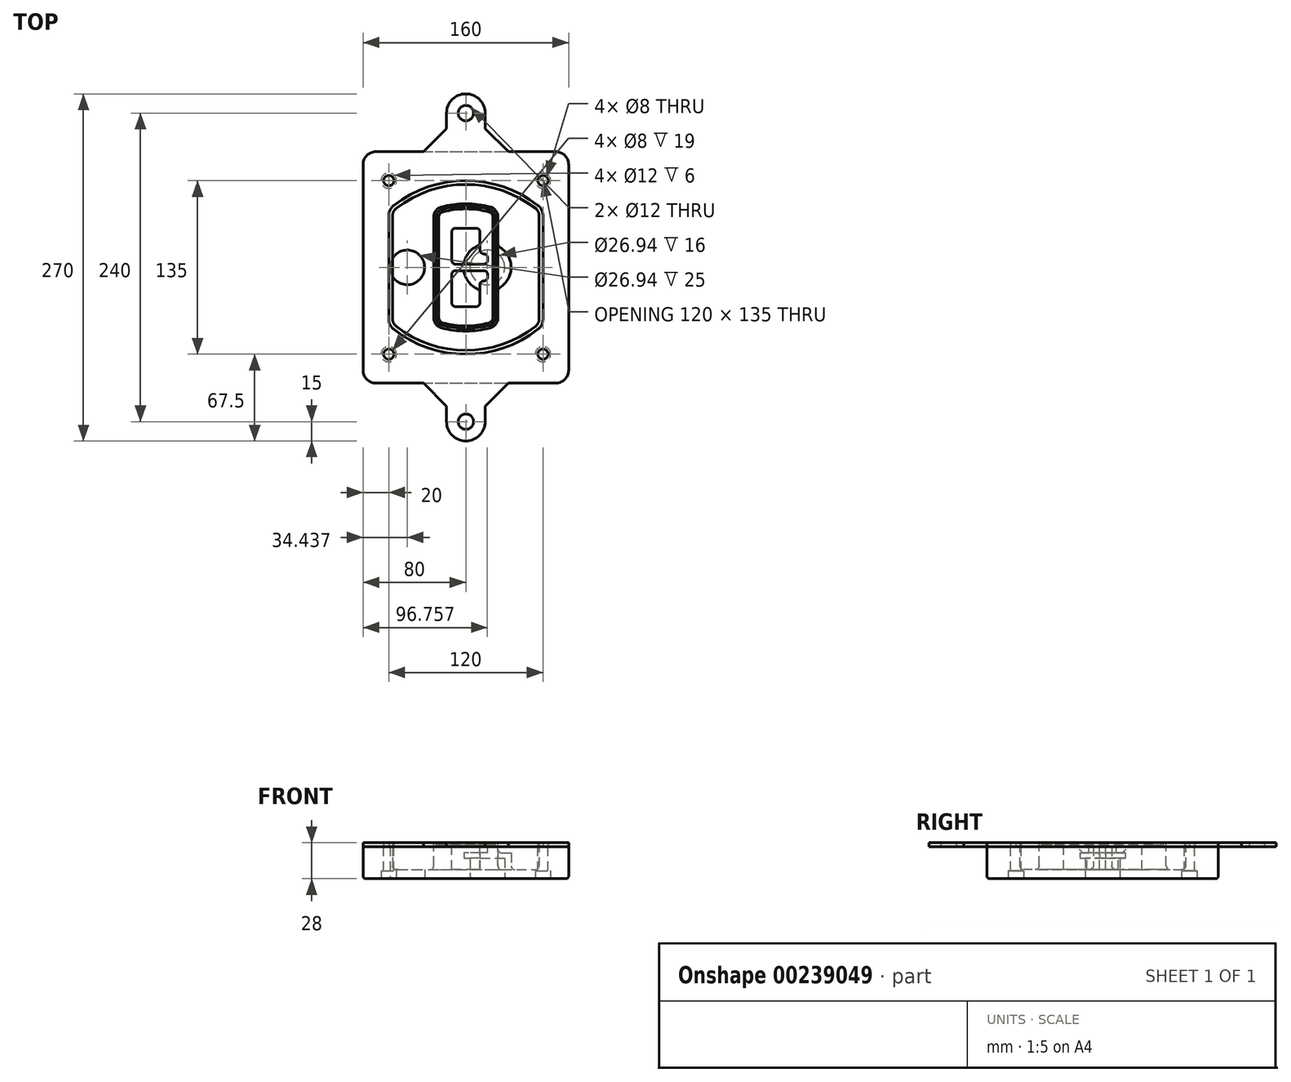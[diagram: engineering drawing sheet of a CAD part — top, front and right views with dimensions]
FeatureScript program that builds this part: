
annotation { "Feature Type Name" : "Feature", "Feature Type Description" : "" }
export const myFeature = defineFeature(function(context is Context, id is Id, definition is map)
    precondition{}
    {
        {
            var Q0;
            Q0=qCreatedBy(makeId("Top.planeOp"),FACE);
            var sketch = newSketch(context, id + "F0", { "sketchPlane" : qUnion([Q0])});
            skPoint(sketch, "E0.rect.middle", {"position": v(0, 0) * mm});
            skLineSegment(sketch, "E1.bottom", {"start": v(-70, -90) * mm, "end": v(70, -90) * mm});
            skLineSegment(sketch, "E1.top", {"start": v(-70, 90) * mm, "end": v(70, 90) * mm});
            skLineSegment(sketch, "E1.left", {"start": v(-80, -80) * mm, "end": v(-80, 80) * mm});
            skLineSegment(sketch, "E1.right", {"start": v(80, -80) * mm, "end": v(80, 80) * mm});
            skLineSegment(sketch, "E2", {"start": v(-80, 90) * mm, "end": v(80, -90) * mm, "construction": true});
            skLineSegment(sketch, "E3", {"start": v(80, 90) * mm, "end": v(-80, -90) * mm, "construction": true});
            skCircle(sketch, "E4", {"center": v(-60, 67.5) * mm, "radius": 4 * mm});
            skCircle(sketch, "E5", {"center": v(60, 67.5) * mm, "radius": 4 * mm});
            skCircle(sketch, "E6", {"center": v(60, -67.5) * mm, "radius": 4 * mm});
            skCircle(sketch, "E7", {"center": v(-60, -67.5) * mm, "radius": 4 * mm});
            skLineSegment(sketch, "E8", {"start": v(-60, 67.5) * mm, "end": v(60, 67.5) * mm, "construction": true});
            skLineSegment(sketch, "E9", {"start": v(60, 67.5) * mm, "end": v(60, -67.5) * mm, "construction": true});
            skLineSegment(sketch, "E10", {"start": v(60, -67.5) * mm, "end": v(-60, -67.5) * mm, "construction": true});
            skLineSegment(sketch, "E11", {"start": v(-60, -67.5) * mm, "end": v(-60, 67.5) * mm, "construction": true});
            skLineSegment(sketch, "E12", {"start": v(-60, 40.3) * mm, "end": v(-60, -40.3) * mm});
            skLineSegment(sketch, "E13", {"start": v(60, 40.3) * mm, "end": v(60, -40.3) * mm});
            skArc(sketch, "E14", {"start": v(56.15, 48.18) * mm, "mid": v(0, 67.5) * mm, "end": v(-56.15, 48.18) * mm});
            skArc(sketch, "E15", {"start": v(-56.15, -48.18) * mm, "mid": v(0, -67.5) * mm, "end": v(56.15, -48.18) * mm});
            skLineSegment(sketch, "E16", {"start": v(-60, 0) * mm, "end": v(60, 0) * mm, "construction": true});
            skPoint(sketch, "E17.visualSharp", {"position": v(-60, -45) * mm});
            skArc(sketch, "E17.filletArc", {"start": v(-60, -40.3) * mm, "mid": v(-58.99, -44.68) * mm, "end": v(-56.15, -48.18) * mm});
            skPoint(sketch, "E18.visualSharp", {"position": v(-60, 45) * mm});
            skArc(sketch, "E18.filletArc", {"start": v(-56.15, 48.18) * mm, "mid": v(-58.99, 44.68) * mm, "end": v(-60, 40.3) * mm});
            skPoint(sketch, "E19.visualSharp", {"position": v(60, 45) * mm});
            skArc(sketch, "E19.filletArc", {"start": v(60, 40.3) * mm, "mid": v(58.99, 44.68) * mm, "end": v(56.15, 48.18) * mm});
            skPoint(sketch, "E20.visualSharp", {"position": v(60, -45) * mm});
            skArc(sketch, "E20.filletArc", {"start": v(56.15, -48.18) * mm, "mid": v(58.99, -44.68) * mm, "end": v(60, -40.3) * mm});
            skPoint(sketch, "E21.visualSharp", {"position": v(-80, 90) * mm});
            skArc(sketch, "E21.filletArc", {"start": v(-70, 90) * mm, "mid": v(-77.07, 87.07) * mm, "end": v(-80, 80) * mm});
            skPoint(sketch, "E22.visualSharp", {"position": v(80, 90) * mm});
            skArc(sketch, "E22.filletArc", {"start": v(80, 80) * mm, "mid": v(77.07, 87.07) * mm, "end": v(70, 90) * mm});
            skPoint(sketch, "E23.visualSharp", {"position": v(80, -90) * mm});
            skArc(sketch, "E23.filletArc", {"start": v(70, -90) * mm, "mid": v(77.07, -87.07) * mm, "end": v(80, -80) * mm});
            skPoint(sketch, "E24.visualSharp", {"position": v(-80, -90) * mm});
            skArc(sketch, "E24.filletArc", {"start": v(-80, -80) * mm, "mid": v(-77.07, -87.07) * mm, "end": v(-70, -90) * mm});
            skArc(sketch, "E25.0", {"start": v(57, 40.3) * mm, "mid": v(56.3, 43.36) * mm, "end": v(54.3, 45.81) * mm});
            skLineSegment(sketch, "E25.1", {"start": v(57, 40.3) * mm, "end": v(57, -40.3) * mm});
            skArc(sketch, "E25.2", {"start": v(54.3, -45.81) * mm, "mid": v(56.3, -43.36) * mm, "end": v(57, -40.3) * mm});
            skArc(sketch, "E25.3", {"start": v(-54.3, -45.81) * mm, "mid": v(0, -64.5) * mm, "end": v(54.3, -45.81) * mm});
            skArc(sketch, "E25.4", {"start": v(-57, -40.3) * mm, "mid": v(-56.3, -43.36) * mm, "end": v(-54.3, -45.81) * mm});
            skArc(sketch, "E25.5", {"start": v(54.3, 45.81) * mm, "mid": v(0, 64.5) * mm, "end": v(-54.3, 45.81) * mm});
            skLineSegment(sketch, "E25.6", {"start": v(-57, 40.3) * mm, "end": v(-57, -40.3) * mm});
            skArc(sketch, "E25.7", {"start": v(-54.3, 45.81) * mm, "mid": v(-56.3, 43.36) * mm, "end": v(-57, 40.3) * mm});
            skArc(sketch, "E26.0", {"start": v(-58.62, 51.33) * mm, "mid": v(-62.58, 46.43) * mm, "end": v(-64, 40.3) * mm});
            skArc(sketch, "E26.1", {"start": v(58.62, 51.33) * mm, "mid": v(0, 71.5) * mm, "end": v(-58.62, 51.33) * mm});
            skArc(sketch, "E26.2", {"start": v(64, 40.3) * mm, "mid": v(62.58, 46.43) * mm, "end": v(58.62, 51.33) * mm});
            skLineSegment(sketch, "E26.3", {"start": v(64, 40.3) * mm, "end": v(64, -40.3) * mm});
            skArc(sketch, "E26.4", {"start": v(58.62, -51.33) * mm, "mid": v(62.58, -46.43) * mm, "end": v(64, -40.3) * mm});
            skLineSegment(sketch, "E26.5", {"start": v(-64, 40.3) * mm, "end": v(-64, -40.3) * mm});
            skArc(sketch, "E26.6", {"start": v(-58.62, -51.33) * mm, "mid": v(0, -71.5) * mm, "end": v(58.62, -51.33) * mm});
            skArc(sketch, "E26.7", {"start": v(-64, -40.3) * mm, "mid": v(-62.58, -46.43) * mm, "end": v(-58.62, -51.33) * mm});
            skSolve(sketch);
        }
        {
            var Q0;
            Q0=makeQuery(id+"F0.imprint","IMPRINT",FACE,{"disambiguationData":[TD([[makeQuery(id+"F0.imprint","IMPRINT",EDGE,{"derivedFrom":sQuery(id+"F0.wireOp",EDGE,"E1.bottom")}),1.0]])]});
            var Q1;
            Q1=makeQuery(id+"F0.imprint","IMPRINT",FACE,{"disambiguationData":[TD([[makeQuery(id+"F0.imprint","IMPRINT",EDGE,{"derivedFrom":sQuery(id+"F0.wireOp",EDGE,"E12")}),1.0]])]});
            var Q2;
            Q2=makeQuery(id+"F0.imprint","IMPRINT",FACE,{"disambiguationData":[TD([[makeQuery(id+"F0.imprint","IMPRINT",EDGE,{"derivedFrom":sQuery(id+"F0.wireOp",EDGE,"E25.0")}),1.0]])]});
            var Q3;
            Q3=makeQuery(id+"F0.imprint","IMPRINT",FACE,{"disambiguationData":[TD([[makeQuery(id+"F0.imprint","IMPRINT",EDGE,{"derivedFrom":sQuery(id+"F0.wireOp",EDGE,"E12")}),-1.0]])]});
            extrude(context, id + "F1", {"entities" : qUnion([Q0, Q1, Q2, Q3]), "oppositeDirection" : true, "depth" : 25 * mm});
        }
        {
            var Q0;
            Q0=makeQuery(id+"F0.imprint","IMPRINT",FACE,{"disambiguationData":[TD([[makeQuery(id+"F0.imprint","IMPRINT",EDGE,{"derivedFrom":sQuery(id+"F0.wireOp",EDGE,"E12")}),1.0]])]});
            extrude(context, id + "F2", {"entities" : qUnion([Q0]), "operationType" : NewBodyOperationType.ADD, "depth" : 3 * mm});
        }
        {
            var Q0;
            Q0=makeQuery(id+"F0.imprint","IMPRINT",FACE,{"disambiguationData":[TD([[makeQuery(id+"F0.imprint","IMPRINT",EDGE,{"derivedFrom":sQuery(id+"F0.wireOp",EDGE,"E25.0")}),1.0]])]});
            extrude(context, id + "F3", {"entities" : qUnion([Q0]), "operationType" : NewBodyOperationType.REMOVE, "oppositeDirection" : true, "depth" : 18 * mm});
        }
        {
            var Q0;
            Q0=makeQuery(id+"F2.opExtrude","CAP_FACE",FACE,{"disambiguationData":[OSD([sQuery(id+"F0.wireOp",EDGE,"E12"),sQuery(id+"F0.wireOp",EDGE,"E13"),sQuery(id+"F0.wireOp",EDGE,"E14"),sQuery(id+"F0.wireOp",EDGE,"E15"),sQuery(id+"F0.wireOp",EDGE,"E17.filletArc"),sQuery(id+"F0.wireOp",EDGE,"E18.filletArc"),sQuery(id+"F0.wireOp",EDGE,"E19.filletArc"),sQuery(id+"F0.wireOp",EDGE,"E20.filletArc"),sQuery(id+"F0.wireOp",EDGE,"E25.0"),sQuery(id+"F0.wireOp",EDGE,"E25.1"),sQuery(id+"F0.wireOp",EDGE,"E25.2"),sQuery(id+"F0.wireOp",EDGE,"E25.3"),sQuery(id+"F0.wireOp",EDGE,"E25.4"),sQuery(id+"F0.wireOp",EDGE,"E25.5"),sQuery(id+"F0.wireOp",EDGE,"E25.6"),sQuery(id+"F0.wireOp",EDGE,"E25.7")])],"isStart":false});
            var sketch = newSketch(context, id + "F4", { "sketchPlane" : qUnion([Q0])});
            skArc(sketch, "E27.0", {"start": v(-19.08, -46.97) * mm, "mid": v(0, -49.5) * mm, "end": v(19.08, -46.97) * mm});
            skArc(sketch, "E28.0", {"start": v(19.08, 46.97) * mm, "mid": v(0, 49.5) * mm, "end": v(-19.08, 46.97) * mm});
            skLineSegment(sketch, "E29", {"start": v(-25, 39.25) * mm, "end": v(-25, -39.25) * mm});
            skLineSegment(sketch, "E30", {"start": v(25, 39.25) * mm, "end": v(25, -39.25) * mm});
            skLineSegment(sketch, "E31", {"start": v(-25, 45.1) * mm, "end": v(25, 45.1) * mm, "construction": true});
            skLineSegment(sketch, "E32", {"start": v(-25, -45.1) * mm, "end": v(25, -45.1) * mm, "construction": true});
            skPoint(sketch, "E33.visualSharp", {"position": v(-25, 45.1) * mm});
            skArc(sketch, "E33.filletArc", {"start": v(-19.08, 46.97) * mm, "mid": v(-23.35, 44.11) * mm, "end": v(-25, 39.25) * mm});
            skPoint(sketch, "E34.visualSharp", {"position": v(25, 45.1) * mm});
            skArc(sketch, "E34.filletArc", {"start": v(25, 39.25) * mm, "mid": v(23.35, 44.11) * mm, "end": v(19.08, 46.97) * mm});
            skPoint(sketch, "E35.visualSharp", {"position": v(25, -45.1) * mm});
            skArc(sketch, "E35.filletArc", {"start": v(19.08, -46.97) * mm, "mid": v(23.35, -44.11) * mm, "end": v(25, -39.25) * mm});
            skPoint(sketch, "E36.visualSharp", {"position": v(-25, -45.1) * mm});
            skArc(sketch, "E36.filletArc", {"start": v(-25, -39.25) * mm, "mid": v(-23.35, -44.11) * mm, "end": v(-19.08, -46.97) * mm});
            skArc(sketch, "E37.0", {"start": v(54.3, 45.81) * mm, "mid": v(0, 64.5) * mm, "end": v(-54.3, 45.81) * mm});
            skArc(sketch, "E37.1", {"start": v(-54.3, 45.81) * mm, "mid": v(-56.3, 43.36) * mm, "end": v(-57, 40.3) * mm});
            skLineSegment(sketch, "E37.2", {"start": v(-57, 40.3) * mm, "end": v(-57, -40.3) * mm});
            skArc(sketch, "E37.3", {"start": v(-57, -40.3) * mm, "mid": v(-56.3, -43.36) * mm, "end": v(-54.3, -45.81) * mm});
            skArc(sketch, "E37.4", {"start": v(-54.3, -45.81) * mm, "mid": v(0, -64.5) * mm, "end": v(54.3, -45.81) * mm});
            skArc(sketch, "E37.5", {"start": v(54.3, -45.81) * mm, "mid": v(56.3, -43.36) * mm, "end": v(57, -40.3) * mm});
            skLineSegment(sketch, "E37.6", {"start": v(57, 40.3) * mm, "end": v(57, -40.3) * mm});
            skArc(sketch, "E37.7", {"start": v(57, 40.3) * mm, "mid": v(56.3, 43.36) * mm, "end": v(54.3, 45.81) * mm});
            skLineSegment(sketch, "E38.0", {"start": v(23, 39.25) * mm, "end": v(23, -39.25) * mm});
            skArc(sketch, "E38.1", {"start": v(18.56, -45.04) * mm, "mid": v(21.76, -42.9) * mm, "end": v(23, -39.25) * mm});
            skArc(sketch, "E38.2", {"start": v(-18.56, -45.04) * mm, "mid": v(0, -47.5) * mm, "end": v(18.56, -45.04) * mm});
            skArc(sketch, "E38.3", {"start": v(-23, -39.25) * mm, "mid": v(-21.76, -42.9) * mm, "end": v(-18.56, -45.04) * mm});
            skLineSegment(sketch, "E38.4", {"start": v(-23, 39.25) * mm, "end": v(-23, -39.25) * mm});
            skArc(sketch, "E38.5", {"start": v(23, 39.25) * mm, "mid": v(21.76, 42.9) * mm, "end": v(18.56, 45.04) * mm});
            skArc(sketch, "E38.6", {"start": v(-18.56, 45.04) * mm, "mid": v(-21.76, 42.9) * mm, "end": v(-23, 39.25) * mm});
            skArc(sketch, "E38.7", {"start": v(18.56, 45.04) * mm, "mid": v(0, 47.5) * mm, "end": v(-18.56, 45.04) * mm});
            skArc(sketch, "E39.0", {"start": v(21, 39.25) * mm, "mid": v(20.18, 41.68) * mm, "end": v(18.04, 43.1) * mm});
            skLineSegment(sketch, "E39.1", {"start": v(21, 39.25) * mm, "end": v(21, -39.25) * mm});
            skArc(sketch, "E39.2", {"start": v(18.04, -43.1) * mm, "mid": v(20.18, -41.68) * mm, "end": v(21, -39.25) * mm});
            skArc(sketch, "E39.3", {"start": v(-18.04, -43.1) * mm, "mid": v(0, -45.5) * mm, "end": v(18.04, -43.1) * mm});
            skArc(sketch, "E39.4", {"start": v(-21, -39.25) * mm, "mid": v(-20.18, -41.68) * mm, "end": v(-18.04, -43.1) * mm});
            skArc(sketch, "E39.5", {"start": v(18.04, 43.1) * mm, "mid": v(0, 45.5) * mm, "end": v(-18.04, 43.1) * mm});
            skLineSegment(sketch, "E39.6", {"start": v(-21, 39.25) * mm, "end": v(-21, -39.25) * mm});
            skArc(sketch, "E39.7", {"start": v(-18.04, 43.1) * mm, "mid": v(-20.18, 41.68) * mm, "end": v(-21, 39.25) * mm});
            skLineSegment(sketch, "E40", {"start": v(-25, 0) * mm, "end": v(25, 0) * mm, "construction": true});
            skLineSegment(sketch, "E41", {"start": v(-11, 5.5) * mm, "end": v(-11, 27.5) * mm});
            skLineSegment(sketch, "E42", {"start": v(-8, 30.5) * mm, "end": v(8, 30.5) * mm});
            skLineSegment(sketch, "E43", {"start": v(11, 27.5) * mm, "end": v(11, 13.5) * mm});
            skLineSegment(sketch, "E44", {"start": v(14, 10.5) * mm, "end": v(14, 10.5) * mm});
            skLineSegment(sketch, "E45", {"start": v(17, 7.5) * mm, "end": v(17, 5.5) * mm});
            skLineSegment(sketch, "E46", {"start": v(14, 2.5) * mm, "end": v(-8, 2.5) * mm});
            skPoint(sketch, "E47.visualSharp", {"position": v(-11, 30.5) * mm});
            skArc(sketch, "E47.filletArc", {"start": v(-8, 30.5) * mm, "mid": v(-10.12, 29.62) * mm, "end": v(-11, 27.5) * mm});
            skPoint(sketch, "E48.visualSharp", {"position": v(11, 30.5) * mm});
            skArc(sketch, "E48.filletArc", {"start": v(11, 27.5) * mm, "mid": v(10.12, 29.62) * mm, "end": v(8, 30.5) * mm});
            skPoint(sketch, "E49.visualSharp", {"position": v(11, 10.5) * mm});
            skArc(sketch, "E49.filletArc", {"start": v(11, 13.5) * mm, "mid": v(11.88, 11.38) * mm, "end": v(14, 10.5) * mm});
            skPoint(sketch, "E50.visualSharp", {"position": v(17, 10.5) * mm});
            skArc(sketch, "E50.filletArc", {"start": v(17, 7.5) * mm, "mid": v(16.12, 9.62) * mm, "end": v(14, 10.5) * mm});
            skPoint(sketch, "E51.visualSharp", {"position": v(17, 2.5) * mm});
            skArc(sketch, "E51.filletArc", {"start": v(14, 2.5) * mm, "mid": v(16.12, 3.38) * mm, "end": v(17, 5.5) * mm});
            skPoint(sketch, "E52.visualSharp", {"position": v(-11, 2.5) * mm});
            skArc(sketch, "E52.filletArc", {"start": v(-11, 5.5) * mm, "mid": v(-10.12, 3.38) * mm, "end": v(-8, 2.5) * mm});
            skLineSegment(sketch, "E53.0.MirrorCS", {"start": v(14, -2.5) * mm, "end": v(-8, -2.5) * mm});
            skArc(sketch, "E54.0.MirrorCS", {"start": v(-11, -5.5) * mm, "mid": v(-10.12, -3.38) * mm, "end": v(-8, -2.5) * mm});
            skLineSegment(sketch, "E55.0.MirrorCS", {"start": v(-11, -5.5) * mm, "end": v(-11, -27.5) * mm});
            skArc(sketch, "E56.0.MirrorCS", {"start": v(-8, -30.5) * mm, "mid": v(-10.12, -29.62) * mm, "end": v(-11, -27.5) * mm});
            skLineSegment(sketch, "E57.0.MirrorCS", {"start": v(-8, -30.5) * mm, "end": v(8, -30.5) * mm});
            skArc(sketch, "E58.0.MirrorCS", {"start": v(11, -27.5) * mm, "mid": v(10.12, -29.62) * mm, "end": v(8, -30.5) * mm});
            skLineSegment(sketch, "E59.0.MirrorCS", {"start": v(11, -27.5) * mm, "end": v(11, -13.5) * mm});
            skArc(sketch, "E60.0.MirrorCS", {"start": v(11, -13.5) * mm, "mid": v(11.88, -11.38) * mm, "end": v(14, -10.5) * mm});
            skArc(sketch, "E61.0.MirrorCS", {"start": v(17, -7.5) * mm, "mid": v(16.12, -9.62) * mm, "end": v(14, -10.5) * mm});
            skLineSegment(sketch, "E62.0.MirrorCS", {"start": v(17, -7.5) * mm, "end": v(17, -5.5) * mm});
            skArc(sketch, "E63.0.MirrorCS", {"start": v(14, -2.5) * mm, "mid": v(16.12, -3.38) * mm, "end": v(17, -5.5) * mm});
            skSolve(sketch);
        }
        {
            var Q0;
            Q0=makeQuery(id+"F4.imprint","IMPRINT",FACE,{"disambiguationData":[TD([[makeQuery(id+"F4.imprint","IMPRINT",EDGE,{"derivedFrom":sQuery(id+"F4.wireOp",EDGE,"E27.0")}),1.0]])]});
            var Q1;
            Q1=makeQuery(id+"F4.imprint","IMPRINT",FACE,{"disambiguationData":[TD([[makeQuery(id+"F4.imprint","IMPRINT",EDGE,{"derivedFrom":sQuery(id+"F4.wireOp",EDGE,"E38.0")}),-1.0]])]});
            var Q2;
            Q2=makeQuery(id+"F4.imprint","IMPRINT",FACE,{"disambiguationData":[TD([[makeQuery(id+"F4.imprint","IMPRINT",EDGE,{"derivedFrom":sQuery(id+"F4.wireOp",EDGE,"E39.0")}),1.0]])]});
            extrude(context, id + "F5", {"entities" : qUnion([Q0, Q1, Q2]), "operationType" : NewBodyOperationType.ADD, "endBound" : BoundingType.UP_TO_NEXT, "oppositeDirection" : true, "depth" : 25 * mm});
        }
        {
            var Q0;
            Q0=makeQuery(id+"F4.imprint","IMPRINT",FACE,{"disambiguationData":[TD([[makeQuery(id+"F4.imprint","IMPRINT",EDGE,{"derivedFrom":sQuery(id+"F4.wireOp",EDGE,"E38.0")}),-1.0]])]});
            extrude(context, id + "F6", {"entities" : qUnion([Q0]), "operationType" : NewBodyOperationType.REMOVE, "oppositeDirection" : true, "depth" : 2 * mm});
        }
        {
            var Q0;
            Q0=makeQuery(id+"F1.opExtrude","CAP_FACE",FACE,{"disambiguationData":[OSD([sQuery(id+"F0.wireOp",EDGE,"E1.bottom"),sQuery(id+"F0.wireOp",EDGE,"E1.top"),sQuery(id+"F0.wireOp",EDGE,"E1.left"),sQuery(id+"F0.wireOp",EDGE,"E1.right"),sQuery(id+"F0.wireOp",EDGE,"E4"),sQuery(id+"F0.wireOp",EDGE,"E5"),sQuery(id+"F0.wireOp",EDGE,"E6"),sQuery(id+"F0.wireOp",EDGE,"E7"),sQuery(id+"F0.wireOp",EDGE,"E21.filletArc"),sQuery(id+"F0.wireOp",EDGE,"E22.filletArc"),sQuery(id+"F0.wireOp",EDGE,"E23.filletArc"),sQuery(id+"F0.wireOp",EDGE,"E24.filletArc")])],"isStart":false});
            var sketch = newSketch(context, id + "F7", { "sketchPlane" : qUnion([Q0])});
            skCircle(sketch, "E64", {"center": v(16.76, 0) * mm, "radius": 13.47 * mm});
            skCircle(sketch, "E65", {"center": v(-45.56, 0) * mm, "radius": 13.47 * mm});
            skLineSegment(sketch, "E66", {"start": v(80, 0) * mm, "end": v(-80, 0) * mm});
            skCircle(sketch, "E67", {"center": v(16.76, 0) * mm, "radius": 18.47 * mm});
            skCircle(sketch, "E68", {"center": v(60, -67.5) * mm, "radius": 6 * mm});
            skCircle(sketch, "E69", {"center": v(-60, -67.5) * mm, "radius": 6 * mm});
            skCircle(sketch, "E70", {"center": v(-60, 67.5) * mm, "radius": 6 * mm});
            skCircle(sketch, "E71", {"center": v(60, 67.5) * mm, "radius": 6 * mm});
            skSolve(sketch);
        }
        {
            var Q0;
            {var subQ1=sQuery(id+"F7.wireOp",EDGE,"E66");var subQ4=sQuery(id+"F7.wireOp",EDGE,"E64");var subQ6=makeQuery(id+"F7.imprint","INTERSECT",VERTEX,{"disambiguationData":[OD(0.0)],"derivedFrom":[subQ4,subQ1]});Q0=makeQuery(id+"F7.imprint","IMPRINT",FACE,{"disambiguationData":[TD([[makeQuery(id+"F7.imprint","IMPRINT",EDGE,{"disambiguationData":[TD([[subQ6,-1.0]])],"derivedFrom":subQ4}),-1.0]])]});}
            var Q1;
            {var subQ0=sQuery(id+"F7.wireOp",EDGE,"E66");var subQ1=sQuery(id+"F7.wireOp",EDGE,"E64");var subQ3=makeQuery(id+"F7.imprint","INTERSECT",VERTEX,{"disambiguationData":[OD(0.0)],"derivedFrom":[subQ1,subQ0]});Q1=makeQuery(id+"F7.imprint","IMPRINT",FACE,{"disambiguationData":[TD([[makeQuery(id+"F7.imprint","IMPRINT",EDGE,{"disambiguationData":[TD([[subQ3,-1.0]])],"derivedFrom":subQ1}),1.0]])]});}
            var Q2;
            {var subQ0=sQuery(id+"F7.wireOp",EDGE,"E66");var subQ1=sQuery(id+"F7.wireOp",EDGE,"E64");var subQ3=makeQuery(id+"F7.imprint","INTERSECT",VERTEX,{"disambiguationData":[OD(0.0)],"derivedFrom":[subQ1,subQ0]});Q2=makeQuery(id+"F7.imprint","IMPRINT",FACE,{"disambiguationData":[TD([[makeQuery(id+"F7.imprint","IMPRINT",EDGE,{"disambiguationData":[TD([[subQ3,1.0]])],"derivedFrom":subQ1}),1.0]])]});}
            var Q3;
            {var subQ1=sQuery(id+"F7.wireOp",EDGE,"E66");var subQ4=sQuery(id+"F7.wireOp",EDGE,"E64");var subQ6=makeQuery(id+"F7.imprint","INTERSECT",VERTEX,{"disambiguationData":[OD(0.0)],"derivedFrom":[subQ4,subQ1]});Q3=makeQuery(id+"F7.imprint","IMPRINT",FACE,{"disambiguationData":[TD([[makeQuery(id+"F7.imprint","IMPRINT",EDGE,{"disambiguationData":[TD([[subQ6,1.0]])],"derivedFrom":subQ4}),-1.0]])]});}
            extrude(context, id + "F8", {"entities" : qUnion([Q0, Q1, Q2, Q3]), "operationType" : NewBodyOperationType.ADD, "oppositeDirection" : true, "depth" : 20 * mm});
        }
        {
            var Q0;
            {var subQ0=sQuery(id+"F7.wireOp",EDGE,"E66");var subQ1=sQuery(id+"F7.wireOp",EDGE,"E64");var subQ3=makeQuery(id+"F7.imprint","INTERSECT",VERTEX,{"disambiguationData":[OD(0.0)],"derivedFrom":[subQ1,subQ0]});Q0=makeQuery(id+"F7.imprint","IMPRINT",FACE,{"disambiguationData":[TD([[makeQuery(id+"F7.imprint","IMPRINT",EDGE,{"disambiguationData":[TD([[subQ3,-1.0]])],"derivedFrom":subQ1}),1.0]])]});}
            var Q1;
            {var subQ0=sQuery(id+"F7.wireOp",EDGE,"E66");var subQ1=sQuery(id+"F7.wireOp",EDGE,"E64");var subQ3=makeQuery(id+"F7.imprint","INTERSECT",VERTEX,{"disambiguationData":[OD(0.0)],"derivedFrom":[subQ1,subQ0]});Q1=makeQuery(id+"F7.imprint","IMPRINT",FACE,{"disambiguationData":[TD([[makeQuery(id+"F7.imprint","IMPRINT",EDGE,{"disambiguationData":[TD([[subQ3,1.0]])],"derivedFrom":subQ1}),1.0]])]});}
            extrude(context, id + "F9", {"entities" : qUnion([Q0, Q1]), "operationType" : NewBodyOperationType.REMOVE, "oppositeDirection" : true, "depth" : 16 * mm});
        }
        {
            var Q0;
            {var subQ0=sQuery(id+"F7.wireOp",EDGE,"E66");var subQ1=sQuery(id+"F7.wireOp",EDGE,"E65");var subQ3=makeQuery(id+"F7.imprint","INTERSECT",VERTEX,{"disambiguationData":[OD(0.0)],"derivedFrom":[subQ1,subQ0]});Q0=makeQuery(id+"F7.imprint","IMPRINT",FACE,{"disambiguationData":[TD([[makeQuery(id+"F7.imprint","IMPRINT",EDGE,{"disambiguationData":[TD([[subQ3,-1.0]])],"derivedFrom":subQ1}),1.0]])]});}
            var Q1;
            {var subQ0=sQuery(id+"F7.wireOp",EDGE,"E66");var subQ1=sQuery(id+"F7.wireOp",EDGE,"E65");var subQ3=makeQuery(id+"F7.imprint","INTERSECT",VERTEX,{"disambiguationData":[OD(0.0)],"derivedFrom":[subQ1,subQ0]});Q1=makeQuery(id+"F7.imprint","IMPRINT",FACE,{"disambiguationData":[TD([[makeQuery(id+"F7.imprint","IMPRINT",EDGE,{"disambiguationData":[TD([[subQ3,1.0]])],"derivedFrom":subQ1}),1.0]])]});}
            extrude(context, id + "F10", {"entities" : qUnion([Q0, Q1]), "operationType" : NewBodyOperationType.REMOVE, "oppositeDirection" : true, "depth" : 25 * mm});
        }
        {
            var Q0;
            Q0=makeQuery(id+"F7.imprint","IMPRINT",FACE,{"disambiguationData":[TD([[makeQuery(id+"F7.imprint","IMPRINT",EDGE,{"derivedFrom":sQuery(id+"F7.wireOp",EDGE,"E68")}),1.0]])]});
            var Q1;
            Q1=makeQuery(id+"F7.imprint","IMPRINT",FACE,{"disambiguationData":[TD([[makeQuery(id+"F7.imprint","IMPRINT",EDGE,{"derivedFrom":makeQuery(id+"F1.opExtrude","CAP_EDGE",EDGE,{"disambiguationData":[OSD([sQuery(id+"F0.wireOp",EDGE,"E5")])],"isStart":false})}),-1.0]])]});
            var Q2;
            Q2=makeQuery(id+"F7.imprint","IMPRINT",FACE,{"disambiguationData":[TD([[makeQuery(id+"F7.imprint","IMPRINT",EDGE,{"derivedFrom":sQuery(id+"F7.wireOp",EDGE,"E69")}),1.0]])]});
            var Q3;
            Q3=makeQuery(id+"F7.imprint","IMPRINT",FACE,{"disambiguationData":[TD([[makeQuery(id+"F7.imprint","IMPRINT",EDGE,{"derivedFrom":makeQuery(id+"F1.opExtrude","CAP_EDGE",EDGE,{"disambiguationData":[OSD([sQuery(id+"F0.wireOp",EDGE,"E4")])],"isStart":false})}),-1.0]])]});
            var Q4;
            Q4=makeQuery(id+"F7.imprint","IMPRINT",FACE,{"disambiguationData":[TD([[makeQuery(id+"F7.imprint","IMPRINT",EDGE,{"derivedFrom":sQuery(id+"F7.wireOp",EDGE,"E70")}),1.0]])]});
            var Q5;
            Q5=makeQuery(id+"F7.imprint","IMPRINT",FACE,{"disambiguationData":[TD([[makeQuery(id+"F7.imprint","IMPRINT",EDGE,{"derivedFrom":makeQuery(id+"F1.opExtrude","CAP_EDGE",EDGE,{"disambiguationData":[OSD([sQuery(id+"F0.wireOp",EDGE,"E7")])],"isStart":false})}),-1.0]])]});
            var Q6;
            Q6=makeQuery(id+"F7.imprint","IMPRINT",FACE,{"disambiguationData":[TD([[makeQuery(id+"F7.imprint","IMPRINT",EDGE,{"derivedFrom":sQuery(id+"F7.wireOp",EDGE,"E71")}),1.0]])]});
            var Q7;
            Q7=makeQuery(id+"F7.imprint","IMPRINT",FACE,{"disambiguationData":[TD([[makeQuery(id+"F7.imprint","IMPRINT",EDGE,{"derivedFrom":makeQuery(id+"F1.opExtrude","CAP_EDGE",EDGE,{"disambiguationData":[OSD([sQuery(id+"F0.wireOp",EDGE,"E6")])],"isStart":false})}),-1.0]])]});
            extrude(context, id + "F11", {"entities" : qUnion([Q0, Q1, Q2, Q3, Q4, Q5, Q6, Q7]), "operationType" : NewBodyOperationType.REMOVE, "oppositeDirection" : true, "depth" : 6 * mm});
        }
        {
            var Q0;
            Q0=makeQuery(id+"F9.boolean.opBoolean","COPY",FACE,{"derivedFrom":makeQuery(id+"F9.opExtrude","CAP_FACE",FACE,{"disambiguationData":[OSD([sQuery(id+"F7.wireOp",EDGE,"E64")])],"isStart":false})});
            var sketch = newSketch(context, id + "F12", { "sketchPlane" : qUnion([Q0])});
            skArc(sketch, "E72.0", {"start": v(11, 17.55) * mm, "mid": v(2.57, 11.82) * mm, "end": v(-1.54, 2.5) * mm});
            skArc(sketch, "E72.1", {"start": v(-1.54, -2.5) * mm, "mid": v(2.57, -11.82) * mm, "end": v(11, -17.55) * mm});
            skLineSegment(sketch, "E73", {"start": v(-1.54, -2.5) * mm, "end": v(14, -2.5) * mm});
            skLineSegment(sketch, "E74.0", {"start": v(14, 2.5) * mm, "end": v(-1.54, 2.5) * mm});
            skArc(sketch, "E74.1", {"start": v(14, 2.5) * mm, "mid": v(16.12, 3.38) * mm, "end": v(17, 5.5) * mm});
            skLineSegment(sketch, "E74.2", {"start": v(17, 7.5) * mm, "end": v(17, 5.5) * mm});
            skArc(sketch, "E74.3", {"start": v(17, 7.5) * mm, "mid": v(16.12, 9.62) * mm, "end": v(14, 10.5) * mm});
            skArc(sketch, "E74.4", {"start": v(11, 13.5) * mm, "mid": v(11.88, 11.38) * mm, "end": v(14, 10.5) * mm});
            skLineSegment(sketch, "E74.5", {"start": v(11, 17.55) * mm, "end": v(11, 13.5) * mm});
            skLineSegment(sketch, "E74.7", {"start": v(14, -2.5) * mm, "end": v(-1.54, -2.5) * mm});
            skArc(sketch, "E74.8", {"start": v(14, -2.5) * mm, "mid": v(16.12, -3.38) * mm, "end": v(17, -5.5) * mm});
            skLineSegment(sketch, "E74.9", {"start": v(17, -7.5) * mm, "end": v(17, -5.5) * mm});
            skArc(sketch, "E74.10", {"start": v(17, -7.5) * mm, "mid": v(16.12, -9.62) * mm, "end": v(14, -10.5) * mm});
            skArc(sketch, "E74.11", {"start": v(11, -13.5) * mm, "mid": v(11.88, -11.38) * mm, "end": v(14, -10.5) * mm});
            skLineSegment(sketch, "E74.12", {"start": v(11, -17.55) * mm, "end": v(11, -13.5) * mm});
            skPoint(sketch, "E75.orphan", {"position": v(11, -27.5) * mm});
            skPoint(sketch, "E76.orphan", {"position": v(-8, -2.5) * mm});
            skPoint(sketch, "E77.orphan", {"position": v(-8, 2.5) * mm});
            skPoint(sketch, "E78.orphan", {"position": v(11, 27.5) * mm});
            skSolve(sketch);
        }
        {
            var Q0;
            {var subQ7=sQuery(id+"F12.wireOp",EDGE,"E72.0");var subQ14=sQuery(id+"F12.wireOp",EDGE,"E72.1");var subQ16=sQuery(id+"F12.wireOp",EDGE,"E74.1");var subQ18=sQuery(id+"F12.wireOp",EDGE,"E74.8");Q0=qUnion([makeQuery(id+"F12.imprint","IMPRINT",FACE,{"disambiguationData":[TD([[makeQuery(id+"F12.imprint","IMPRINT",EDGE,{"derivedFrom":subQ7}),1.0]])]}),makeQuery(id+"F12.imprint","IMPRINT",FACE,{"disambiguationData":[TD([[makeQuery(id+"F12.imprint","IMPRINT",EDGE,{"derivedFrom":subQ14}),1.0]])]}),makeQuery(id+"F12.imprint","IMPRINT",FACE,{"disambiguationData":[TD([[makeQuery(id+"F12.imprint","IMPRINT",EDGE,{"derivedFrom":subQ16}),1.0]])]}),makeQuery(id+"F12.imprint","IMPRINT",FACE,{"disambiguationData":[TD([[makeQuery(id+"F12.imprint","IMPRINT",EDGE,{"derivedFrom":subQ18}),-1.0]])]})]);}
            var Q1;
            Q1=makeQuery(id+"F5.boolean.opBoolean","SPLIT",FACE,{"disambiguationData":[TD([makeQuery(id+"F5.opExtrude","SWEPT_FACE",FACE,{"disambiguationData":[OSD([sQuery(id+"F4.wireOp",EDGE,"E41")])]})])],"derivedFrom":makeQuery(id+"F3.boolean.opBoolean","COPY",FACE,{"derivedFrom":makeQuery(id+"F3.opExtrude","CAP_FACE",FACE,{"disambiguationData":[OSD([sQuery(id+"F0.wireOp",EDGE,"E25.0"),sQuery(id+"F0.wireOp",EDGE,"E25.1"),sQuery(id+"F0.wireOp",EDGE,"E25.2"),sQuery(id+"F0.wireOp",EDGE,"E25.3"),sQuery(id+"F0.wireOp",EDGE,"E25.4"),sQuery(id+"F0.wireOp",EDGE,"E25.5"),sQuery(id+"F0.wireOp",EDGE,"E25.6"),sQuery(id+"F0.wireOp",EDGE,"E25.7")])],"isStart":false})})});
            extrude(context, id + "F13", {"entities" : qUnion([Q0]), "operationType" : NewBodyOperationType.REMOVE, "endBound" : BoundingType.UP_TO_SURFACE, "endBoundEntityFace" : qUnion([Q1]), "depth" : 25 * mm});
        }
        {
            var Q0;
            Q0=makeQuery(id+"F3.boolean.opBoolean","COPY",EDGE,{"derivedFrom":makeQuery(id+"F3.opExtrude","CAP_EDGE",EDGE,{"disambiguationData":[OSD([sQuery(id+"F0.wireOp",EDGE,"E25.6")])],"isStart":false})});
            var Q1;
            Q1=makeQuery(id+"F8.boolean.opBoolean","INTERSECT",EDGE,{"derivedFrom":[makeQuery(id+"F5.opExtrude","SWEPT_FACE",FACE,{"disambiguationData":[OSD([sQuery(id+"F4.wireOp",EDGE,"E30")])]}),makeQuery(id+"F8.opExtrude","CAP_FACE",FACE,{"disambiguationData":[OSD([sQuery(id+"F7.wireOp",EDGE,"E67")])],"isStart":false})]});
            var Q2;
            Q2=makeQuery(id+"F8.boolean.opBoolean","INTERSECT",EDGE,{"disambiguationData":[OD(1.0)],"derivedFrom":[makeQuery(id+"F5.opExtrude","SWEPT_FACE",FACE,{"disambiguationData":[OSD([sQuery(id+"F4.wireOp",EDGE,"E30")])]}),makeQuery(id+"F8.opExtrude","SWEPT_FACE",FACE,{"disambiguationData":[OSD([sQuery(id+"F7.wireOp",EDGE,"E67")])]})]});
            var Q3;
            {var subQ0=sQuery(id+"F4.wireOp",EDGE,"E30");Q3=makeQuery(id+"F8.boolean.opBoolean","SPLIT",EDGE,{"disambiguationData":[TD([makeQuery(id+"F5.opExtrude","SWEPT_FACE",FACE,{"disambiguationData":[OSD([sQuery(id+"F4.wireOp",EDGE,"E35.filletArc")])]})])],"derivedFrom":makeQuery(id+"F5.opExtrude","CAP_EDGE",EDGE,{"disambiguationData":[OSD([subQ0])],"isStart":false})});}
            var Q4;
            {var subQ0=sQuery(id+"F0.wireOp",EDGE,"E25.7");var subQ1=sQuery(id+"F0.wireOp",EDGE,"E25.1");var subQ2=sQuery(id+"F0.wireOp",EDGE,"E25.6");var subQ3=sQuery(id+"F0.wireOp",EDGE,"E25.5");var subQ4=sQuery(id+"F0.wireOp",EDGE,"E25.4");var subQ5=sQuery(id+"F0.wireOp",EDGE,"E25.0");var subQ6=sQuery(id+"F0.wireOp",EDGE,"E25.2");var subQ7=sQuery(id+"F0.wireOp",EDGE,"E25.3");Q4=makeQuery(id+"F8.boolean.opBoolean","INTERSECT",EDGE,{"derivedFrom":[makeQuery(id+"F5.boolean.opBoolean","SPLIT",FACE,{"disambiguationData":[TD([makeQuery(id+"F2.opExtrude","SWEPT_FACE",FACE,{"disambiguationData":[OSD([subQ5])]})])],"derivedFrom":makeQuery(id+"F3.boolean.opBoolean","COPY",FACE,{"derivedFrom":makeQuery(id+"F3.opExtrude","CAP_FACE",FACE,{"disambiguationData":[OSD([subQ5,subQ1,subQ6,subQ7,subQ4,subQ3,subQ2,subQ0])],"isStart":false})})}),makeQuery(id+"F8.opExtrude","SWEPT_FACE",FACE,{"disambiguationData":[OSD([sQuery(id+"F7.wireOp",EDGE,"E67")])]})]});}
            var Q5;
            Q5=makeQuery(id+"F8.boolean.opBoolean","INTERSECT",EDGE,{"disambiguationData":[OD(0.0)],"derivedFrom":[makeQuery(id+"F5.opExtrude","SWEPT_FACE",FACE,{"disambiguationData":[OSD([sQuery(id+"F4.wireOp",EDGE,"E30")])]}),makeQuery(id+"F8.opExtrude","SWEPT_FACE",FACE,{"disambiguationData":[OSD([sQuery(id+"F7.wireOp",EDGE,"E67")])]})]});
            fillet(context, id + "F14", {"entities" : qUnion([Q0, Q1, Q2, Q3, Q4, Q5]), "radius" : 3 * mm, "tangentPropagation" : true, "allowEdgeOverflow" : false});
        }
        {
            var Q0;
            Q0=makeQuery(id+"F1.opExtrude","CAP_EDGE",EDGE,{"disambiguationData":[OSD([sQuery(id+"F0.wireOp",EDGE,"E1.bottom")])],"isStart":false});
            fillet(context, id + "F15", {"entities" : qUnion([Q0]), "radius" : 2 * mm, "tangentPropagation" : true, "allowEdgeOverflow" : false});
        }
        {
            var Q0;
            {var subQ0=sQuery(id+"F0.wireOp",EDGE,"E22.filletArc");var subQ1=sQuery(id+"F0.wireOp",EDGE,"E7");var subQ2=sQuery(id+"F0.wireOp",EDGE,"E6");var subQ3=sQuery(id+"F0.wireOp",EDGE,"E5");var subQ4=sQuery(id+"F0.wireOp",EDGE,"E4");var subQ5=sQuery(id+"F0.wireOp",EDGE,"E1.bottom");var subQ6=sQuery(id+"F0.wireOp",EDGE,"E21.filletArc");var subQ7=sQuery(id+"F0.wireOp",EDGE,"E1.top");var subQ8=sQuery(id+"F0.wireOp",EDGE,"E1.left");var subQ9=sQuery(id+"F0.wireOp",EDGE,"E1.right");var subQ10=sQuery(id+"F0.wireOp",EDGE,"E23.filletArc");var subQ11=sQuery(id+"F0.wireOp",EDGE,"E24.filletArc");Q0=makeQuery(id+"F2.boolean.opBoolean","SPLIT",FACE,{"disambiguationData":[TD([makeQuery(id+"F1.opExtrude","SWEPT_FACE",FACE,{"disambiguationData":[OSD([subQ5])]})])],"derivedFrom":makeQuery(id+"F1.opExtrude","CAP_FACE",FACE,{"disambiguationData":[OSD([subQ5,subQ7,subQ8,subQ9,subQ4,subQ3,subQ2,subQ1,subQ6,subQ0,subQ10,subQ11])],"isStart":true})});}
            var sketch = newSketch(context, id + "F16", { "sketchPlane" : qUnion([Q0])});
            skLineSegment(sketch, "E79", {"start": v(0, 90) * mm, "end": v(0, 120) * mm, "construction": true});
            skCircle(sketch, "E80", {"center": v(0, 120) * mm, "radius": 6 * mm});
            skArc(sketch, "E81", {"start": v(15, 120) * mm, "mid": v(0, 135) * mm, "end": v(-15, 120) * mm});
            skLineSegment(sketch, "E82", {"start": v(-15, 120) * mm, "end": v(-15, 108) * mm});
            skLineSegment(sketch, "E83", {"start": v(-15, 108) * mm, "end": v(-33, 90) * mm});
            skLineSegment(sketch, "E84", {"start": v(15, 120) * mm, "end": v(15, 108) * mm});
            skLineSegment(sketch, "E85", {"start": v(15, 108) * mm, "end": v(33, 90) * mm});
            skLineSegment(sketch, "E86", {"start": v(-80, 0) * mm, "end": v(80, 0) * mm, "construction": true});
            skLineSegment(sketch, "E87.MirrorCS", {"start": v(-15, -108) * mm, "end": v(-33, -90) * mm});
            skLineSegment(sketch, "E88.MirrorCS", {"start": v(15, -120) * mm, "end": v(15, -108) * mm});
            skCircle(sketch, "E89.MirrorC", {"center": v(0, -120) * mm, "radius": 6 * mm});
            skLineSegment(sketch, "E90.MirrorCS", {"start": v(0, -90) * mm, "end": v(0, -120) * mm, "construction": true});
            skLineSegment(sketch, "E91.MirrorCS", {"start": v(-15, -120) * mm, "end": v(-15, -108) * mm});
            skLineSegment(sketch, "E92.MirrorCS", {"start": v(15, -108) * mm, "end": v(33, -90) * mm});
            skArc(sketch, "E93.MirrorCS", {"start": v(15, -120) * mm, "mid": v(0, -135) * mm, "end": v(-15, -120) * mm});
            skSolve(sketch);
        }
        {
            var Q0;
            Q0=makeQuery(id+"F16.imprint","IMPRINT",FACE,{"disambiguationData":[TD([[makeQuery(id+"F16.imprint","IMPRINT",EDGE,{"derivedFrom":sQuery(id+"F16.wireOp",EDGE,"E80")}),-1.0]])]});
            var Q1;
            Q1=makeQuery(id+"F16.imprint","IMPRINT",FACE,{"disambiguationData":[TD([[makeQuery(id+"F16.imprint","IMPRINT",EDGE,{"derivedFrom":makeQuery(id+"F1.opExtrude","CAP_EDGE",EDGE,{"disambiguationData":[OSD([sQuery(id+"F0.wireOp",EDGE,"E1.left")])],"isStart":true})}),-1.0]])]});
            var Q2;
            {var subQ0=sQuery(id+"F16.wireOp",EDGE,"E87.MirrorCS");Q2=makeQuery(id+"F16.imprint","IMPRINT",FACE,{"disambiguationData":[TD([[makeQuery(id+"F16.imprint","IMPRINT",EDGE,{"derivedFrom":subQ0}),-1.0]])]});}
            var Q3;
            Q3=makeQuery(id+"F2.opExtrude","CAP_FACE",FACE,{"disambiguationData":[OSD([sQuery(id+"F0.wireOp",EDGE,"E12"),sQuery(id+"F0.wireOp",EDGE,"E13"),sQuery(id+"F0.wireOp",EDGE,"E14"),sQuery(id+"F0.wireOp",EDGE,"E15"),sQuery(id+"F0.wireOp",EDGE,"E17.filletArc"),sQuery(id+"F0.wireOp",EDGE,"E18.filletArc"),sQuery(id+"F0.wireOp",EDGE,"E19.filletArc"),sQuery(id+"F0.wireOp",EDGE,"E20.filletArc"),sQuery(id+"F0.wireOp",EDGE,"E25.0"),sQuery(id+"F0.wireOp",EDGE,"E25.1"),sQuery(id+"F0.wireOp",EDGE,"E25.2"),sQuery(id+"F0.wireOp",EDGE,"E25.3"),sQuery(id+"F0.wireOp",EDGE,"E25.4"),sQuery(id+"F0.wireOp",EDGE,"E25.5"),sQuery(id+"F0.wireOp",EDGE,"E25.6"),sQuery(id+"F0.wireOp",EDGE,"E25.7")])],"isStart":false});
            extrude(context, id + "F17", {"entities" : qUnion([Q0, Q1, Q2]), "endBound" : BoundingType.UP_TO_SURFACE, "endBoundEntityFace" : qUnion([Q3]), "depth" : 25 * mm});
        }
    });
